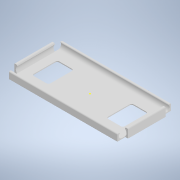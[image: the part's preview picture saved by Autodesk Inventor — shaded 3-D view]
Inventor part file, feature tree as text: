
AUTODESK INVENTOR PART (.ipt)
format: ipt  version: 2020 (Build 240168000, 168)  size: 285,184 bytes
history: native  units: mm
features: sketch x3, extrude x3, fillet x1, other x1
ambient origin geometry x8: Origin, YZ Plane, XZ Plane, XY Plane, X Axis, Y Axis, Z Axis, Center Point
bodies: Body1 (feature_tree)
feature tree (8):
  sketch  "Sketch2"  dims[d85=3600.0mm d86=0.0mm d87=1250.0mm d88=0.0mm]
  extrude  "Extrusion3"  Depth=1250.0mm TaperAngle=0.0deg
  extrude  "Extrusion4"  Depth=420.0mm
  extrude  "Extrusion5"  Depth=840.0mm
  fillet  "Fillet1"  Radius=1200.0mm
  sketch  "Sketch11"  dims[d92=550.0mm d93=380.0mm d94=1200.0mm d95=0.0mm d96=63.5mm d98=957.474029mm d99=957.474029mm d100=550.0mm d132=27.0mm d133=45.0mm d134=36.0mm d135=70.0mm d136=30.0mm d137=33.5mm d138=19.0mm d139=13.0mm d140=24.0mm d141=23.898419mm d145=23.136251mm d151=30.0mm d161=165.0mm d169=30.0mm d174=250.0mm d176=1835.928467mm d177=30.0mm d178=50.0mm d179=20.0mm d324=9.5mm d325=27.0mm d326=50.0mm d327=58.0mm d328=66.0mm d329=34.0mm d330=14.0mm d331=12.5mm d332=840.0mm d333=50.0mm d336=90.0deg d345=3671.856933mm d349=90.0deg d350=220.0mm d0=0.5mm d1=0.872665mm d2=0.5mm d3=0.872665mm d97=0.872665mm d109=0.5mm d110=0.872665mm d111=0.5mm d112=0.872665mm d113=0.872665mm d163=0.5mm d164=0.872665mm d165=0.5mm d166=0.872665mm]
  sketch  "Sketch4"  dims[d90=420.0mm d91=420.0mm]
  other  "Image2"
